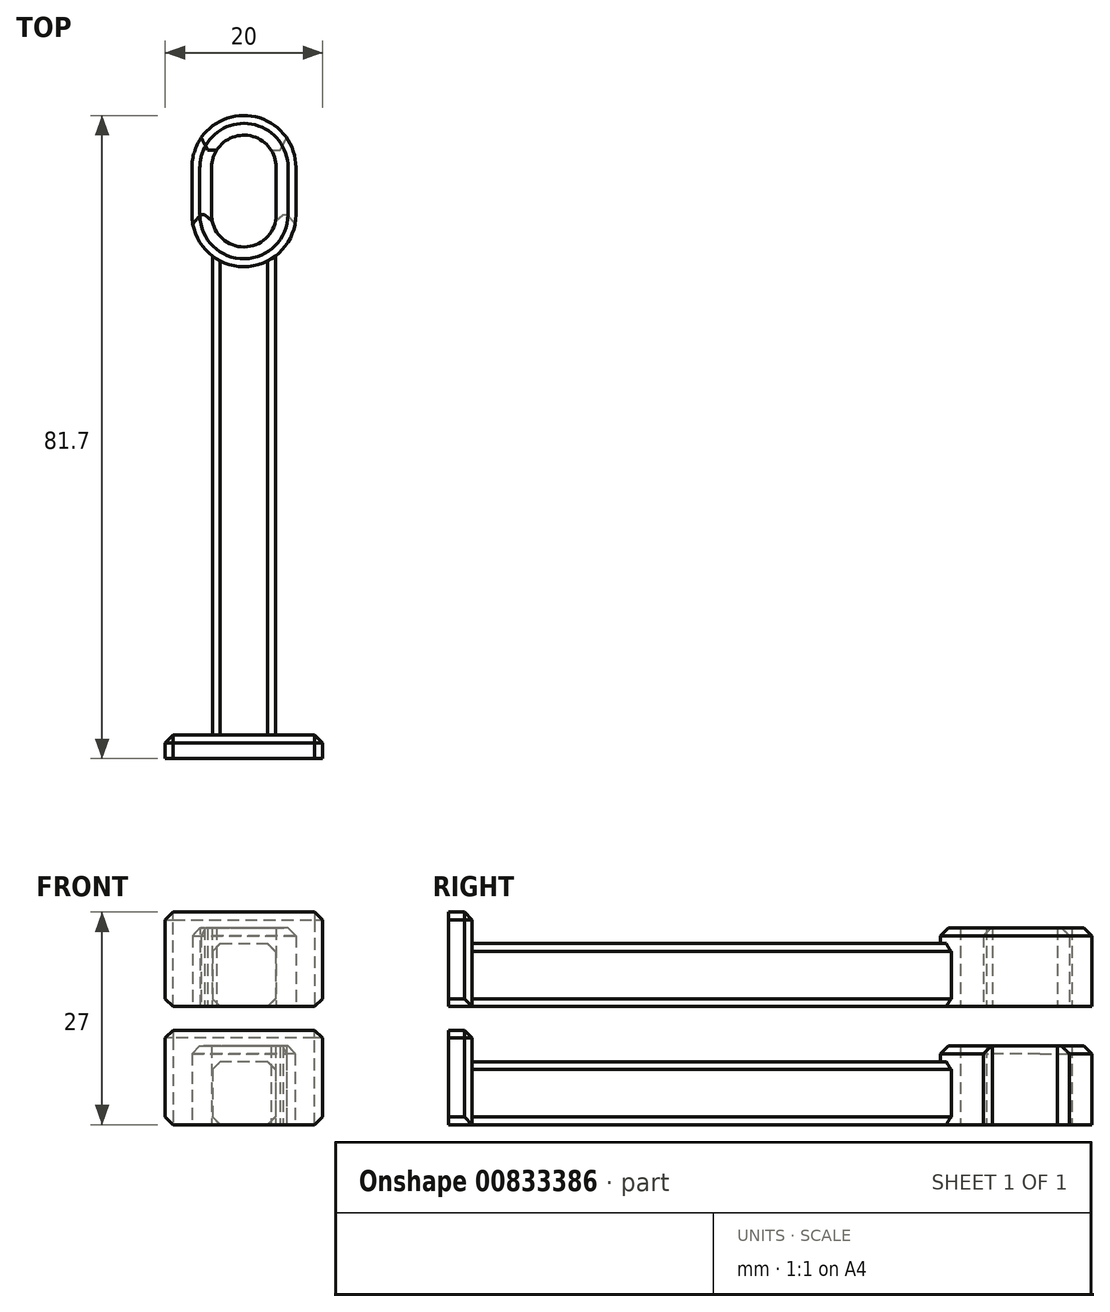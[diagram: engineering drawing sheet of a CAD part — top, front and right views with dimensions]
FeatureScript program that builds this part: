
annotation { "Feature Type Name" : "Feature", "Feature Type Description" : "" }
export const myFeature = defineFeature(function(context is Context, id is Id, definition is map)
    precondition{}
    {
        {
            var Q0;
            Q0=qCreatedBy(makeId("Top.planeOp"),FACE);
            var sketch = newSketch(context, id + "F0", { "sketchPlane" : qUnion([Q0])});
            skArc(sketch, "E0", {"start": v(-4.1, 0) * mm, "mid": v(0, -4.1) * mm, "end": v(4.1, 0) * mm});
            skLineSegment(sketch, "E1", {"start": v(0, 0) * mm, "end": v(0, 6) * mm, "construction": true});
            skArc(sketch, "E2", {"start": v(-3.46, 8.2) * mm, "mid": v(1.15, 9.94) * mm, "end": v(4.1, 6) * mm});
            skLineSegment(sketch, "E3", {"start": v(-3.46, 8.2) * mm, "end": v(-6.22, 8.2) * mm});
            skLineSegment(sketch, "E4", {"start": v(-4.1, 0) * mm, "end": v(-6.6, 0) * mm});
            skLineSegment(sketch, "E5", {"start": v(4.1, 0) * mm, "end": v(4.1, 6) * mm});
            skArc(sketch, "E6", {"start": v(-6.22, 8.2) * mm, "mid": v(1.12, 12.5) * mm, "end": v(6.6, 6) * mm});
            skArc(sketch, "E7", {"start": v(-6.6, 0) * mm, "mid": v(-5.91, -2.93) * mm, "end": v(-4, -5.25) * mm});
            skArc(sketch, "E8", {"start": v(6.6, 0) * mm, "mid": v(5.91, -2.93) * mm, "end": v(4, -5.25) * mm});
            skLineSegment(sketch, "E9", {"start": v(6.6, 0) * mm, "end": v(6.6, 6) * mm});
            skLineSegment(sketch, "E10", {"start": v(4.1, 0) * mm, "end": v(6.6, 0) * mm, "construction": true});
            skLineSegment(sketch, "E11", {"start": v(-4, -5.25) * mm, "end": v(-4, -66.1) * mm});
            skLineSegment(sketch, "E12", {"start": v(-4, -66.1) * mm, "end": v(4, -66.1) * mm});
            skLineSegment(sketch, "E13", {"start": v(4, -66.1) * mm, "end": v(4, -5.25) * mm});
            skLineSegment(sketch, "E14", {"start": v(-4, -5.25) * mm, "end": v(4, -5.25) * mm, "construction": true});
            skLineSegment(sketch, "E15", {"start": v(4, -66.1) * mm, "end": v(10, -66.1) * mm});
            skLineSegment(sketch, "E16", {"start": v(10, -66.1) * mm, "end": v(10, -69.1) * mm});
            skLineSegment(sketch, "E17", {"start": v(10, -69.1) * mm, "end": v(-10, -69.1) * mm});
            skLineSegment(sketch, "E18", {"start": v(-10, -69.1) * mm, "end": v(-10, -66.1) * mm});
            skLineSegment(sketch, "E19", {"start": v(-10, -66.1) * mm, "end": v(-4, -66.1) * mm});
            skArc(sketch, "E20", {"start": v(-4, -5.25) * mm, "mid": v(0, -6.6) * mm, "end": v(4, -5.25) * mm});
            skLineSegment(sketch, "E21", {"start": v(0, -4.1) * mm, "end": v(0, -69.1) * mm, "construction": true});
            skSolve(sketch);
        }
        {
            var Q0;
            Q0=makeQuery(id+"F0.imprint","IMPRINT",FACE,{"disambiguationData":[TD([[makeQuery(id+"F0.imprint","IMPRINT",EDGE,{"derivedFrom":sQuery(id+"F0.wireOp",EDGE,"E11")}),1.0]])]});
            extrude(context, id + "F1", {"entities" : qUnion([Q0]), "depth" : 8 * mm, "offsetDistance" : 25 * mm});
        }
        {
            var Q0;
            Q0=makeQuery(id+"F0.imprint","IMPRINT",FACE,{"disambiguationData":[TD([[makeQuery(id+"F0.imprint","IMPRINT",EDGE,{"derivedFrom":sQuery(id+"F0.wireOp",EDGE,"E12")}),-1.0]])]});
            extrude(context, id + "F2", {"entities" : qUnion([Q0]), "operationType" : NewBodyOperationType.ADD, "depth" : 12 * mm, "offsetDistance" : 25 * mm});
        }
        {
            var Q0;
            Q0=makeQuery(id+"F0.imprint","IMPRINT",FACE,{"disambiguationData":[TD([[makeQuery(id+"F0.imprint","IMPRINT",EDGE,{"derivedFrom":sQuery(id+"F0.wireOp",EDGE,"E0")}),-1.0]])]});
            extrude(context, id + "F3", {"entities" : qUnion([Q0]), "operationType" : NewBodyOperationType.ADD, "depth" : 10 * mm, "offsetDistance" : 25 * mm});
        }
        {
            var Q0;
            Q0=makeQuery(id+"F1.opExtrude","CAP_EDGE",EDGE,{"disambiguationData":[OSD([sQuery(id+"F0.wireOp",EDGE,"E11")])],"isStart":false});
            var Q1;
            Q1=makeQuery(id+"F1.opExtrude","CAP_EDGE",EDGE,{"disambiguationData":[OSD([sQuery(id+"F0.wireOp",EDGE,"E11")])],"isStart":true});
            var Q2;
            Q2=makeQuery(id+"F1.opExtrude","CAP_EDGE",EDGE,{"disambiguationData":[OSD([sQuery(id+"F0.wireOp",EDGE,"E13")])],"isStart":false});
            var Q3;
            Q3=makeQuery(id+"F1.opExtrude","CAP_EDGE",EDGE,{"disambiguationData":[OSD([sQuery(id+"F0.wireOp",EDGE,"E13")])],"isStart":true});
            var Q4;
            Q4=makeQuery(id+"F1.opExtrude","SWEPT_EDGE",EDGE,{"disambiguationData":[OSD([sQuery(id+"F0.wireOp",EDGE,"E11"),sQuery(id+"F0.wireOp",EDGE,"E12"),sQuery(id+"F0.wireOp",EDGE,"E19")])]});
            var Q5;
            Q5=makeQuery(id+"F1.opExtrude","SWEPT_EDGE",EDGE,{"disambiguationData":[OSD([sQuery(id+"F0.wireOp",EDGE,"E0"),sQuery(id+"F0.wireOp",EDGE,"E4")])]});
            var Q6;
            Q6=makeQuery(id+"F1.opExtrude","SWEPT_EDGE",EDGE,{"disambiguationData":[OSD([sQuery(id+"F0.wireOp",EDGE,"E3"),sQuery(id+"F0.wireOp",EDGE,"E6")])]});
            var Q7;
            Q7=makeQuery(id+"F1.opExtrude","SWEPT_EDGE",EDGE,{"disambiguationData":[OSD([sQuery(id+"F0.wireOp",EDGE,"E4"),sQuery(id+"F0.wireOp",EDGE,"E7")])]});
            var Q8;
            Q8=makeQuery(id+"F1.opExtrude","CAP_EDGE",EDGE,{"disambiguationData":[OSD([sQuery(id+"F0.wireOp",EDGE,"E8")])],"isStart":true});
            var Q9;
            Q9=makeQuery(id+"F1.opExtrude","CAP_EDGE",EDGE,{"disambiguationData":[OSD([sQuery(id+"F0.wireOp",EDGE,"E7")])],"isStart":true});
            var Q10;
            Q10=makeQuery(id+"F1.opExtrude","CAP_EDGE",EDGE,{"disambiguationData":[OSD([sQuery(id+"F0.wireOp",EDGE,"E7")])],"isStart":false});
            var Q11;
            Q11=makeQuery(id+"F1.opExtrude","CAP_EDGE",EDGE,{"disambiguationData":[OSD([sQuery(id+"F0.wireOp",EDGE,"E8")])],"isStart":false});
            var Q12;
            Q12=makeQuery(id+"F2.opExtrude","CAP_EDGE",EDGE,{"disambiguationData":[OSD([sQuery(id+"F0.wireOp",EDGE,"E18")])],"isStart":true});
            var Q13;
            Q13=makeQuery(id+"F2.opExtrude","CAP_EDGE",EDGE,{"disambiguationData":[OSD([sQuery(id+"F0.wireOp",EDGE,"E18")])],"isStart":false});
            var Q14;
            Q14=makeQuery(id+"F2.opExtrude","CAP_EDGE",EDGE,{"disambiguationData":[OSD([sQuery(id+"F0.wireOp",EDGE,"E16")])],"isStart":false});
            var Q15;
            Q15=makeQuery(id+"F2.opExtrude","CAP_EDGE",EDGE,{"disambiguationData":[OSD([sQuery(id+"F0.wireOp",EDGE,"E16")])],"isStart":true});
            var Q16;
            Q16=makeQuery(id+"F2.opExtrude","CAP_EDGE",EDGE,{"disambiguationData":[OSD([sQuery(id+"F0.wireOp",EDGE,"E12"),sQuery(id+"F0.wireOp",EDGE,"E15"),sQuery(id+"F0.wireOp",EDGE,"E19")])],"isStart":false});
            var Q17;
            Q17=makeQuery(id+"F2.opExtrude","SWEPT_EDGE",EDGE,{"disambiguationData":[OSD([sQuery(id+"F0.wireOp",EDGE,"E15"),sQuery(id+"F0.wireOp",EDGE,"E16")])]});
            var Q18;
            Q18=makeQuery(id+"F2.opExtrude","SWEPT_EDGE",EDGE,{"disambiguationData":[OSD([sQuery(id+"F0.wireOp",EDGE,"E18"),sQuery(id+"F0.wireOp",EDGE,"E19")])]});
            var Q19;
            Q19=makeQuery(id+"F3.opExtrude","CAP_EDGE",EDGE,{"disambiguationData":[OSD([sQuery(id+"F0.wireOp",EDGE,"E7"),sQuery(id+"F0.wireOp",EDGE,"E8"),sQuery(id+"F0.wireOp",EDGE,"E20")])],"isStart":false});
            var Q20;
            Q20=makeQuery(id+"F3.opExtrude","SWEPT_EDGE",EDGE,{"disambiguationData":[OSD([sQuery(id+"F0.wireOp",EDGE,"E4"),sQuery(id+"F0.wireOp",EDGE,"E7")])]});
            var Q21;
            Q21=makeQuery(id+"F3.opExtrude","SWEPT_EDGE",EDGE,{"disambiguationData":[OSD([sQuery(id+"F0.wireOp",EDGE,"E0"),sQuery(id+"F0.wireOp",EDGE,"E4")])]});
            var Q22;
            Q22=makeQuery(id+"F3.opExtrude","SWEPT_EDGE",EDGE,{"disambiguationData":[OSD([sQuery(id+"F0.wireOp",EDGE,"E3"),sQuery(id+"F0.wireOp",EDGE,"E6")])]});
            var Q23;
            Q23=makeQuery(id+"F1.opExtrude","CAP_EDGE",EDGE,{"disambiguationData":[OSD([sQuery(id+"F0.wireOp",EDGE,"E20")])],"isStart":false});
            chamfer(context, id + "F4", {"entities" : qUnion([Q0, Q1, Q2, Q3, Q4, Q5, Q6, Q7, Q8, Q9, Q10, Q11, Q12, Q13, Q14, Q15, Q16, Q17, Q18, Q19, Q20, Q21, Q22, Q23]), "width" : 1 * mm, "tangentPropagation" : true});
        }
        {
            var Q0;
            Q0=makeQuery(id+"F1.opExtrude","SWEPT_BODY",BODY,{"disambiguationData":[OSD([sQuery(id+"F0.wireOp",EDGE,"E0"),sQuery(id+"F0.wireOp",EDGE,"E2"),sQuery(id+"F0.wireOp",EDGE,"E3"),sQuery(id+"F0.wireOp",EDGE,"E4"),sQuery(id+"F0.wireOp",EDGE,"E5"),sQuery(id+"F0.wireOp",EDGE,"E6"),sQuery(id+"F0.wireOp",EDGE,"E7"),sQuery(id+"F0.wireOp",EDGE,"E8"),sQuery(id+"F0.wireOp",EDGE,"E9"),sQuery(id+"F0.wireOp",EDGE,"E11"),sQuery(id+"F0.wireOp",EDGE,"E12"),sQuery(id+"F0.wireOp",EDGE,"E13")])]});
            var Q1;
            Q1=qCreatedBy(makeId("Top.planeOp"),FACE);
            mirror(context, id + "F5", {"entities" : qUnion([Q0]), "mirrorPlane" : qUnion([Q1])});
        }
        {
            var Q0;
            Q0=makeQuery(id+"F5.opPattern","COPY",BODY,{"derivedFrom":makeQuery(id+"F1.opExtrude","SWEPT_BODY",BODY,{"disambiguationData":[OSD([sQuery(id+"F0.wireOp",EDGE,"E11"),sQuery(id+"F0.wireOp",EDGE,"E12"),sQuery(id+"F0.wireOp",EDGE,"E13"),sQuery(id+"F0.wireOp",EDGE,"E20")])]}),"instanceName":"1"});
            var Q1;
            Q1=sQuery(id+"F0.wireOp",EDGE,"E21");
            transform(context, id + "F6", {"entities" : qUnion([Q0]), "transformType" : TransformType.ROTATION, "transformAxis" : qUnion([Q1]), "angle" : 180 * degree, "makeCopy" : false});
        }
        {
            var Q0;
            Q0=makeQuery(id+"F5.opPattern","COPY",BODY,{"derivedFrom":makeQuery(id+"F1.opExtrude","SWEPT_BODY",BODY,{"disambiguationData":[OSD([sQuery(id+"F0.wireOp",EDGE,"E0"),sQuery(id+"F0.wireOp",EDGE,"E2"),sQuery(id+"F0.wireOp",EDGE,"E3"),sQuery(id+"F0.wireOp",EDGE,"E4"),sQuery(id+"F0.wireOp",EDGE,"E5"),sQuery(id+"F0.wireOp",EDGE,"E6"),sQuery(id+"F0.wireOp",EDGE,"E7"),sQuery(id+"F0.wireOp",EDGE,"E8"),sQuery(id+"F0.wireOp",EDGE,"E9"),sQuery(id+"F0.wireOp",EDGE,"E11"),sQuery(id+"F0.wireOp",EDGE,"E12"),sQuery(id+"F0.wireOp",EDGE,"E13")])]}),"instanceName":"1"});
            transform(context, id + "F7", {"entities" : qUnion([Q0]), "transformType" : TransformType.TRANSLATION_3D, "dx" : 0 * mm, "dy" : 0 * mm, "dz" : -15 * mm, "makeCopy" : false});
        }
    });
